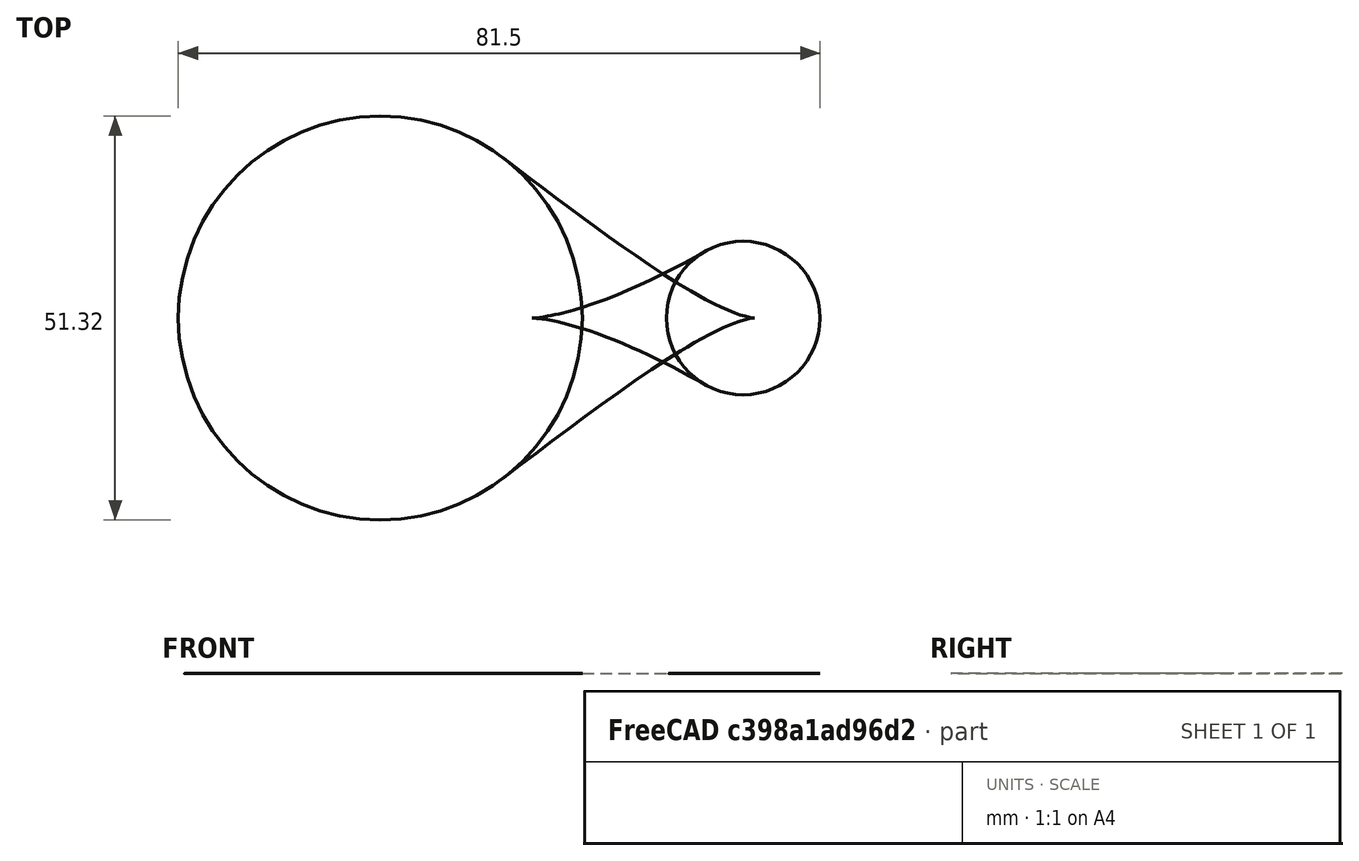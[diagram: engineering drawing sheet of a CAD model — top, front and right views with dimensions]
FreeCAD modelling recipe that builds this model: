
FCSTD DOCUMENT  (FreeCAD 0.21R33771 (Git))
Label: rulledFace
License: All rights reserved
LicenseURL: https://en.wikipedia.org/wiki/All_rights_reserved
objects: Part::RuledSurface×3, Part::Face×2, Sketcher::SketchObject×1, PartDesign::Body×1
note: 7 computed .brp shape members not serialized (recipe doc carries the construction recipe); baked Part::Feature solids carry a one-line shape summary decoded from their .brp

FEATURE [Sketcher::SketchObject] Sketch
  FullyConstrained = false
  MapMode = 5
  Support = -> [XY_Plane]
  sketch-geometry (2):
    g0: Circle CenterX=-35.025 CenterY=17.3877 CenterZ=0 NormalX=0 NormalY=0 NormalZ=1 AngleXU=0 Radius=25.6574
    g1: Circle CenterX=11.0649 CenterY=17.3877 CenterZ=0 NormalX=0 NormalY=0 NormalZ=1 AngleXU=0 Radius=9.75048
FEATURE [PartDesign::Body] Body
  Group = -> [Sketch]
  Origin = -> Origin
FEATURE [Part::Face] Face
  FaceMakerClass = Part::FaceMakerBullseye
  Sources = -> [Sketch]
FEATURE [Part::Face] Face001
  FaceMakerClass = Part::FaceMakerBullseye
  Sources = -> [Sketch]
FEATURE [Part::RuledSurface] Ruled_Surface
  Curve1 = -> Sketch
  Curve2 = -> Sketch
  Orientation = 0
FEATURE [Part::RuledSurface] Ruled_Surface001
  Curve1 = -> Sketch
  Curve2 = -> Sketch
  Orientation = 0
FEATURE [Part::RuledSurface] Ruled_Surface002
  Curve1 = -> Sketch [Edge1]
  Curve2 = -> Sketch [Edge2]
  Orientation = 0
